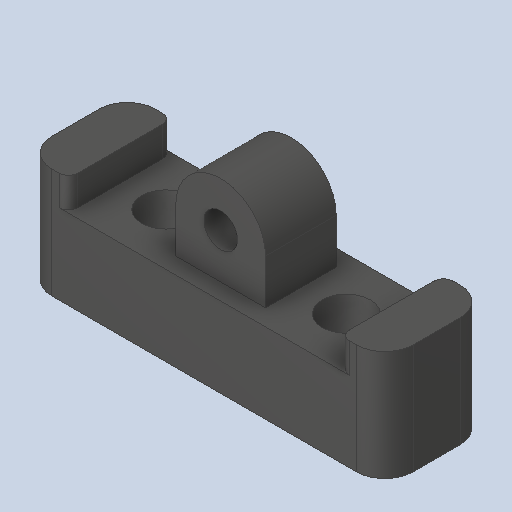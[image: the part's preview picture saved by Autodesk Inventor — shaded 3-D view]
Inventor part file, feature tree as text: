
AUTODESK INVENTOR PART (.ipt)
format: ipt  version: 2023.4 (Build 274418000, 418)  size: 126,976 bytes
history: native  units: in
note: dims shown in document units (in); Inventor stores cm internally (conversion verified against a paired STEP export)
features: fillet x1
ambient origin geometry x8: Origin, YZ Plane, XZ Plane, XY Plane, X Axis, Y Axis, Z Axis, Center Point
bodies: Solid1 (feature_tree)
feature tree (1):
  fillet  "Fillet2"  [1 undecoded]
note: 1 required parameter value undecoded (feature->parameter linkage not recoverable at this tier; creation-order binding heuristic only, values carry confidence <= 0.55)
